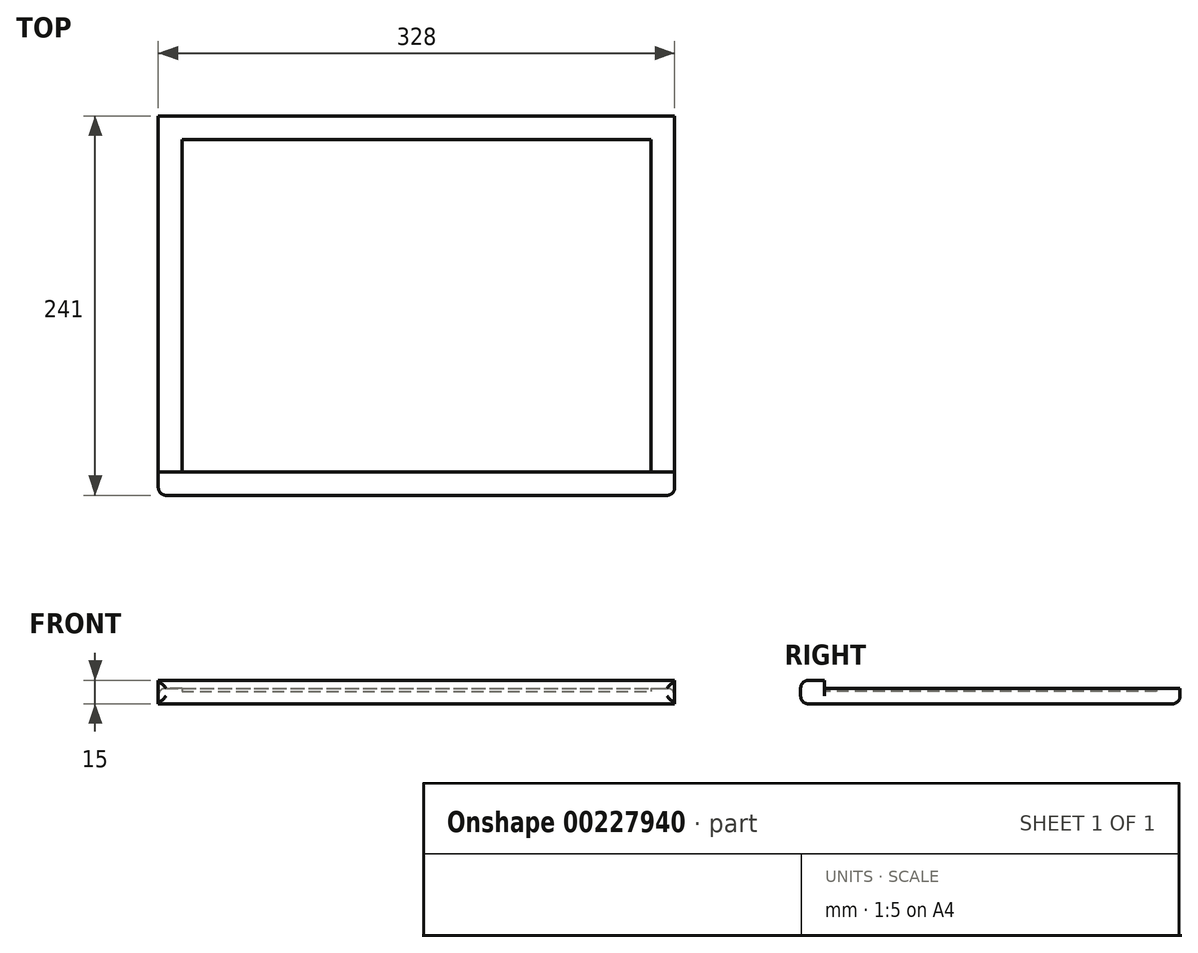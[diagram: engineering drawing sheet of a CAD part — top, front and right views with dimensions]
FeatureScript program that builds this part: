
annotation { "Feature Type Name" : "Feature", "Feature Type Description" : "" }
export const myFeature = defineFeature(function(context is Context, id is Id, definition is map)
    precondition{}
    {
        {
            var Q0;
            Q0=qCreatedBy(makeId("Top.planeOp"),FACE);
            var sketch = newSketch(context, id + "F0", { "sketchPlane" : qUnion([Q0])});
            skLineSegment(sketch, "E0.bottom", {"start": v(-149, 105.5) * mm, "end": v(149, 105.5) * mm});
            skLineSegment(sketch, "E0.top", {"start": v(-149, -105.5) * mm, "end": v(149, -105.5) * mm});
            skLineSegment(sketch, "E0.left", {"start": v(-149, 105.5) * mm, "end": v(-149, -105.5) * mm});
            skLineSegment(sketch, "E0.right", {"start": v(149, 105.5) * mm, "end": v(149, -105.5) * mm});
            skPoint(sketch, "E1", {"position": v(0, 105.5) * mm});
            skPoint(sketch, "E2", {"position": v(-149, 0) * mm});
            skLineSegment(sketch, "E3.0", {"start": v(-164, 120.5) * mm, "end": v(164, 120.5) * mm});
            skLineSegment(sketch, "E3.1", {"start": v(-164, 120.5) * mm, "end": v(-164, -120.5) * mm});
            skLineSegment(sketch, "E3.2", {"start": v(-164, -120.5) * mm, "end": v(164, -120.5) * mm});
            skLineSegment(sketch, "E3.3", {"start": v(164, 120.5) * mm, "end": v(164, -120.5) * mm});
            skLineSegment(sketch, "E4", {"start": v(149, -105.5) * mm, "end": v(164, -105.5) * mm});
            skLineSegment(sketch, "E5", {"start": v(-149, -105.5) * mm, "end": v(-164, -105.5) * mm});
            skSolve(sketch);
        }
        {
            var Q0;
            Q0=makeQuery(id+"F0.imprint","IMPRINT",FACE,{"disambiguationData":[TD([[makeQuery(id+"F0.imprint","IMPRINT",EDGE,{"derivedFrom":sQuery(id+"F0.wireOp",EDGE,"E0.bottom")}),1.0]])]});
            extrude(context, id + "F1", {"entities" : qUnion([Q0]), "depth" : 10 * mm});
        }
        {
            var Q0;
            Q0=makeQuery(id+"F0.imprint","IMPRINT",FACE,{"disambiguationData":[TD([[makeQuery(id+"F0.imprint","IMPRINT",EDGE,{"derivedFrom":sQuery(id+"F0.wireOp",EDGE,"E0.bottom")}),-1.0]])]});
            extrude(context, id + "F2", {"entities" : qUnion([Q0]), "operationType" : NewBodyOperationType.ADD, "depth" : 8 * mm});
        }
        {
            var Q0;
            Q0=makeQuery(id+"F0.imprint","IMPRINT",FACE,{"disambiguationData":[TD([[makeQuery(id+"F0.imprint","IMPRINT",EDGE,{"derivedFrom":sQuery(id+"F0.wireOp",EDGE,"E0.top")}),-1.0]])]});
            extrude(context, id + "F3", {"entities" : qUnion([Q0]), "operationType" : NewBodyOperationType.ADD, "depth" : 15 * mm});
        }
        {
            var Q0;
            Q0=makeQuery(id+"F1.opExtrude","CAP_EDGE",EDGE,{"disambiguationData":[OSD([sQuery(id+"F0.wireOp",EDGE,"E3.0")])],"isStart":true});
            var Q1;
            Q1=makeQuery(id+"F1.opExtrude","CAP_EDGE",EDGE,{"disambiguationData":[OSD([sQuery(id+"F0.wireOp",EDGE,"E3.1")])],"isStart":false});
            var Q2;
            Q2=makeQuery(id+"F1.opExtrude","CAP_EDGE",EDGE,{"disambiguationData":[OSD([sQuery(id+"F0.wireOp",EDGE,"E3.3")])],"isStart":false});
            var Q3;
            Q3=makeQuery(id+"F3.opExtrude","CAP_EDGE",EDGE,{"disambiguationData":[OSD([sQuery(id+"F0.wireOp",EDGE,"E3.2")])],"isStart":false});
            var Q4;
            Q4=makeQuery(id+"F3.opExtrude","SWEPT_EDGE",EDGE,{"disambiguationData":[OSD([sQuery(id+"F0.wireOp",EDGE,"E3.2"),sQuery(id+"F0.wireOp",EDGE,"E3.3")])]});
            var Q5;
            Q5=makeQuery(id+"F3.opExtrude","SWEPT_EDGE",EDGE,{"disambiguationData":[OSD([sQuery(id+"F0.wireOp",EDGE,"E3.1"),sQuery(id+"F0.wireOp",EDGE,"E3.2")])]});
            var Q6;
            Q6=makeQuery(id+"F3.opExtrude","CAP_EDGE",EDGE,{"disambiguationData":[OSD([sQuery(id+"F0.wireOp",EDGE,"E3.2")])],"isStart":true});
            fillet(context, id + "F4", {"entities" : qUnion([Q0, Q1, Q2, Q3, Q4, Q5, Q6]), "radius" : 5 * mm, "tangentPropagation" : true, "allowEdgeOverflow" : false});
        }
    });
